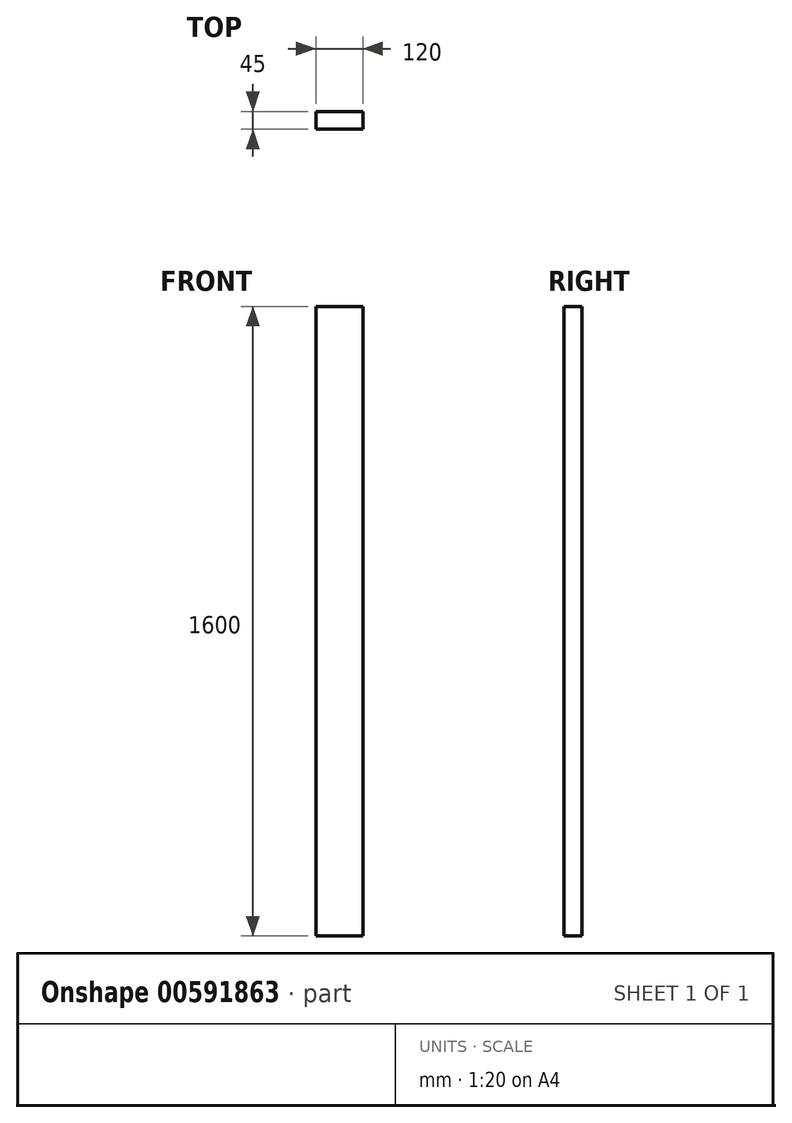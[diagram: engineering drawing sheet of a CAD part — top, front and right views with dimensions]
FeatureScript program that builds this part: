
annotation { "Feature Type Name" : "Feature", "Feature Type Description" : "" }
export const myFeature = defineFeature(function(context is Context, id is Id, definition is map)
    precondition{}
    {
        {
            var Q0;
            Q0=qCreatedBy(makeId("Top.planeOp"),FACE);
            var sketch = newSketch(context, id + "F0", { "sketchPlane" : qUnion([Q0])});
            skLineSegment(sketch, "E0.bottom", {"start": v(0, 0) * mm, "end": v(120, 0) * mm});
            skLineSegment(sketch, "E0.top", {"start": v(0, 45) * mm, "end": v(120, 45) * mm});
            skLineSegment(sketch, "E0.left", {"start": v(0, 0) * mm, "end": v(0, 45) * mm});
            skLineSegment(sketch, "E0.right", {"start": v(120, 0) * mm, "end": v(120, 45) * mm});
            skSolve(sketch);
        }
        {
            var Q0;
            Q0=makeQuery(id+"F0.imprint","IMPRINT",FACE,{"disambiguationData":[TD([[makeQuery(id+"F0.imprint","IMPRINT",EDGE,{"derivedFrom":sQuery(id+"F0.wireOp",EDGE,"E0.bottom")}),1.0]])]});
            extrude(context, id + "F1", {"entities" : qUnion([Q0]), "depth" : 1600 * mm, "offsetDistance" : 25 * mm});
        }
    });
